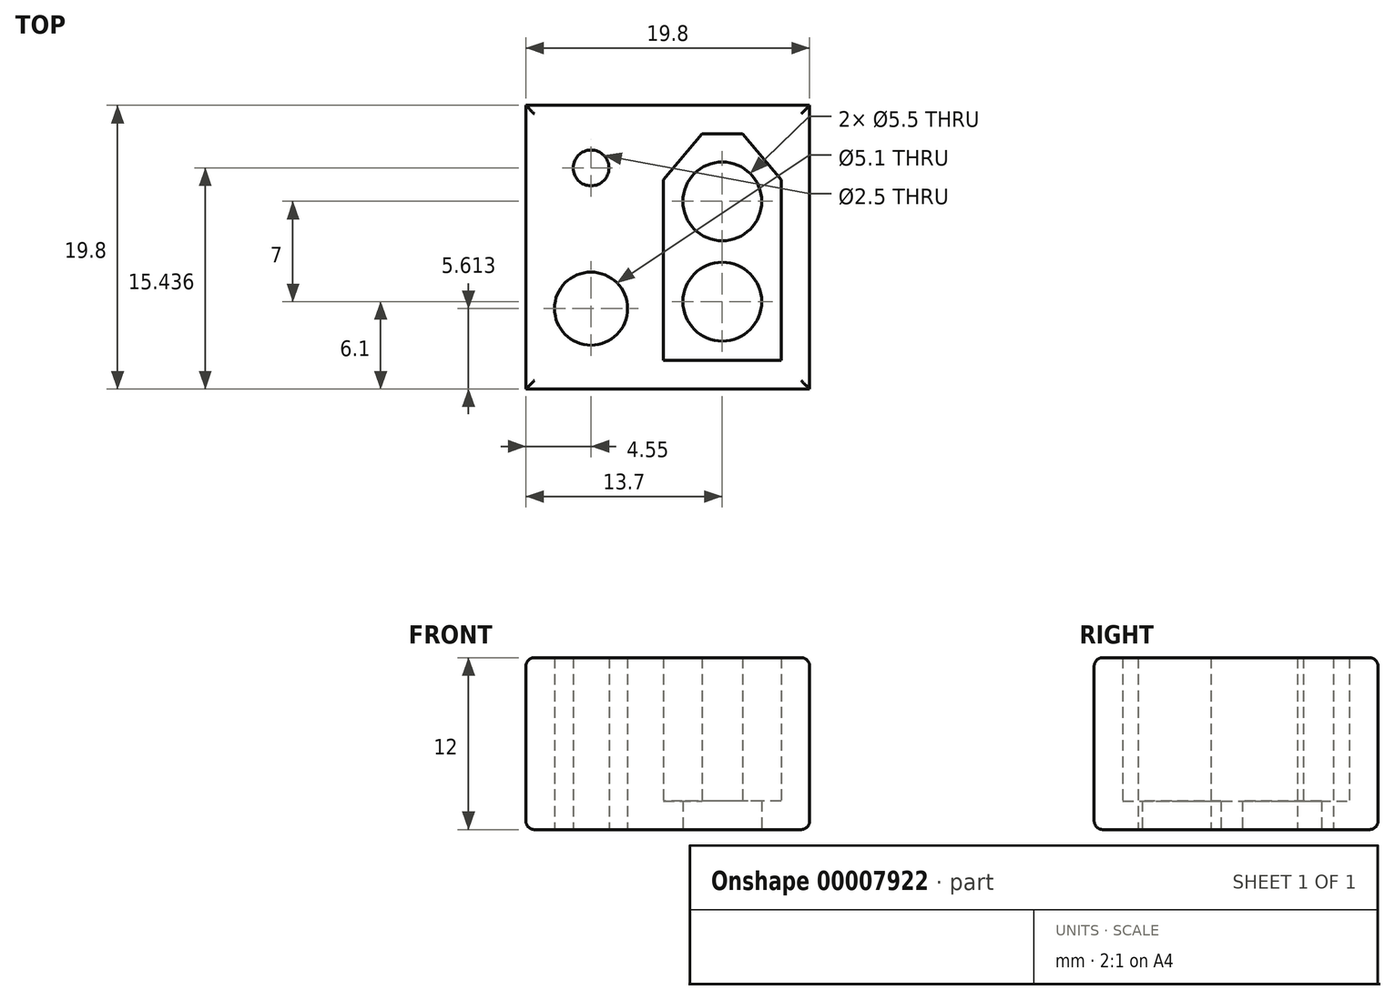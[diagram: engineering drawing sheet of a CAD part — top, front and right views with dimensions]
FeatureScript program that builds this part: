
annotation { "Feature Type Name" : "Feature", "Feature Type Description" : "" }
export const myFeature = defineFeature(function(context is Context, id is Id, definition is map)
    precondition{}
    {
        {
            var Q0;
            Q0=qCreatedBy(makeId("Top.planeOp"),FACE);
            var sketch = newSketch(context, id + "F0", { "sketchPlane" : qUnion([Q0])});
            skLineSegment(sketch, "E0.bottom", {"start": v(0, 0) * mm, "end": v(19.8, 0) * mm});
            skLineSegment(sketch, "E0.top", {"start": v(0, 19.8) * mm, "end": v(19.8, 19.8) * mm});
            skLineSegment(sketch, "E0.left", {"start": v(0, 0) * mm, "end": v(0, 19.8) * mm});
            skLineSegment(sketch, "E0.right", {"start": v(19.8, 0) * mm, "end": v(19.8, 19.8) * mm});
            skLineSegment(sketch, "E1.bottom", {"start": v(17.8, 2) * mm, "end": v(9.6, 2) * mm});
            skLineSegment(sketch, "E1.top", {"start": v(15.1, 17.8) * mm, "end": v(12.3, 17.8) * mm});
            skLineSegment(sketch, "E1.left", {"start": v(17.8, 2) * mm, "end": v(17.8, 14.6) * mm});
            skLineSegment(sketch, "E1.right", {"start": v(9.6, 2) * mm, "end": v(9.6, 14.6) * mm});
            skLineSegment(sketch, "E2", {"start": v(17.8, 14.6) * mm, "end": v(15.1, 17.8) * mm});
            skLineSegment(sketch, "E3", {"start": v(9.6, 14.6) * mm, "end": v(12.3, 17.8) * mm});
            skPoint(sketch, "E4.orphan", {"position": v(17.8, 17.8) * mm});
            skLineSegment(sketch, "E5", {"start": v(13.7, 2) * mm, "end": v(13.7, 24.2) * mm, "construction": true});
            skCircle(sketch, "E6", {"center": v(13.7, 6.1) * mm, "radius": 2.75 * mm});
            skCircle(sketch, "E7", {"center": v(13.7, 13.1) * mm, "radius": 2.75 * mm});
            skLineSegment(sketch, "E8", {"start": v(7.1, 0) * mm, "end": v(7.1, 25.9) * mm, "construction": true});
            skCircle(sketch, "E9", {"center": v(4.55, 5.61) * mm, "radius": 2.55 * mm});
            skLineSegment(sketch, "E10", {"start": v(4.55, 5.61) * mm, "end": v(4.55, 23.27) * mm, "construction": true});
            skCircle(sketch, "E11", {"center": v(4.55, 15.44) * mm, "radius": 1.25 * mm});
            skSolve(sketch);
        }
        {
            var Q0;
            Q0=makeQuery(id+"F0.imprint","IMPRINT",FACE,{"disambiguationData":[TD([[makeQuery(id+"F0.imprint","IMPRINT",EDGE,{"derivedFrom":sQuery(id+"F0.wireOp",EDGE,"E0.bottom")}),1.0]])]});
            extrude(context, id + "F1", {"entities" : qUnion([Q0]), "depth" : 12 * mm});
        }
        {
            var Q0;
            Q0=makeQuery(id+"F0.imprint","IMPRINT",FACE,{"disambiguationData":[TD([[makeQuery(id+"F0.imprint","IMPRINT",EDGE,{"derivedFrom":sQuery(id+"F0.wireOp",EDGE,"E1.bottom")}),-1.0]])]});
            extrude(context, id + "F2", {"entities" : qUnion([Q0]), "operationType" : NewBodyOperationType.ADD, "depth" : 2 * mm});
        }
        {
            var Q0;
            Q0=makeQuery(id+"F1.opExtrude","CAP_EDGE",EDGE,{"disambiguationData":[OSD([sQuery(id+"F0.wireOp",EDGE,"E0.bottom")])],"isStart":false});
            var Q1;
            Q1=makeQuery(id+"F1.opExtrude","CAP_EDGE",EDGE,{"disambiguationData":[OSD([sQuery(id+"F0.wireOp",EDGE,"E0.right")])],"isStart":false});
            var Q2;
            Q2=makeQuery(id+"F1.opExtrude","CAP_EDGE",EDGE,{"disambiguationData":[OSD([sQuery(id+"F0.wireOp",EDGE,"E0.top")])],"isStart":false});
            var Q3;
            Q3=makeQuery(id+"F1.opExtrude","CAP_EDGE",EDGE,{"disambiguationData":[OSD([sQuery(id+"F0.wireOp",EDGE,"E0.left")])],"isStart":false});
            fillet(context, id + "F3", {"entities" : qUnion([Q0, Q1, Q2, Q3]), "radius" : .6 * mm, "tangentPropagation" : true, "allowEdgeOverflow" : false});
        }
        {
            var Q0;
            Q0=makeQuery(id+"F1.opExtrude","CAP_EDGE",EDGE,{"disambiguationData":[OSD([sQuery(id+"F0.wireOp",EDGE,"E0.bottom")])],"isStart":true});
            var Q1;
            Q1=makeQuery(id+"F1.opExtrude","CAP_EDGE",EDGE,{"disambiguationData":[OSD([sQuery(id+"F0.wireOp",EDGE,"E0.right")])],"isStart":true});
            var Q2;
            Q2=makeQuery(id+"F1.opExtrude","CAP_EDGE",EDGE,{"disambiguationData":[OSD([sQuery(id+"F0.wireOp",EDGE,"E0.top")])],"isStart":true});
            var Q3;
            Q3=makeQuery(id+"F1.opExtrude","CAP_EDGE",EDGE,{"disambiguationData":[OSD([sQuery(id+"F0.wireOp",EDGE,"E0.left")])],"isStart":true});
            fillet(context, id + "F4", {"entities" : qUnion([Q0, Q1, Q2, Q3]), "radius" : .6 * mm, "tangentPropagation" : true, "allowEdgeOverflow" : false});
        }
    });
